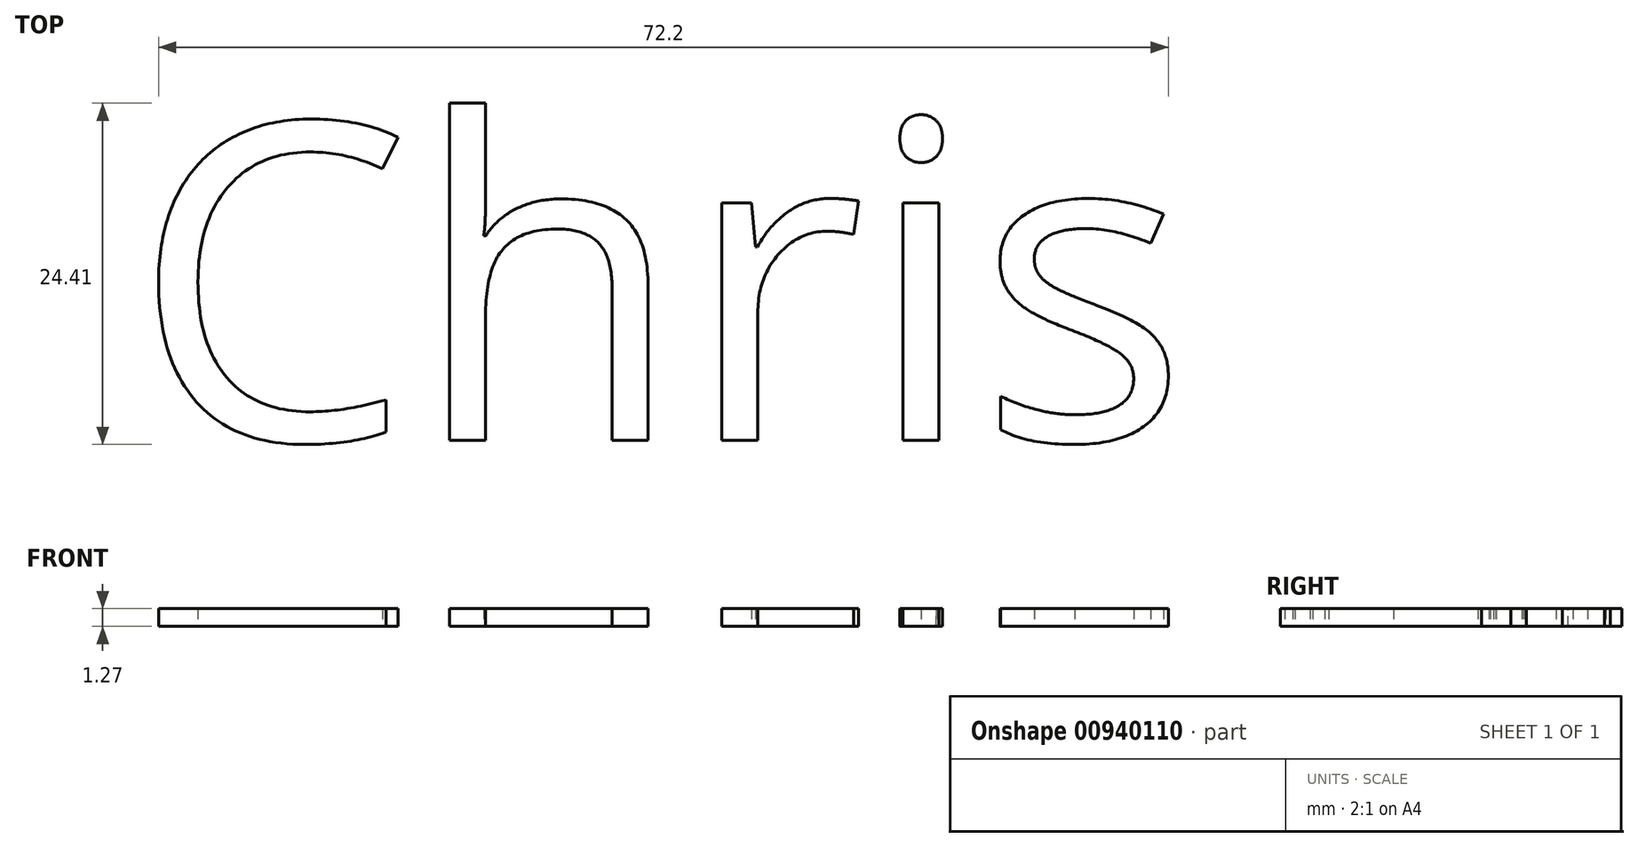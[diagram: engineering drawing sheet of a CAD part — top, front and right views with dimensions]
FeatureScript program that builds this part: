
annotation { "Feature Type Name" : "Feature", "Feature Type Description" : "" }
export const myFeature = defineFeature(function(context is Context, id is Id, definition is map)
    precondition{}
    {
        {
            var Q0;
            Q0=qCreatedBy(makeId("Top.planeOp"),FACE);
            var sketch = newSketch(context, id + "F0", { "sketchPlane" : qUnion([Q0])});
            skText(sketch, "E0", { "text": "Chris", "fontName": "OpenSans-Regular.ttf"});
            const initialGuessF0  = {"E0": [-0.02064, -0.01622, 1, 0, 0.02284]};
            skSetInitialGuess(sketch, initialGuessF0);
            skSolve(sketch);
        }
        {
            var Q0;
            Q0 = qSketchRegion(id + "F0", true);
            var Q1;
            Q1=makeQuery(id+"F0.imprint","IMPRINT",FACE,{"disambiguationData":[TD([[makeQuery(id+"F0.imprint","IMPRINT",EDGE,{"derivedFrom":sQuery(id+"F0.wireOp",EDGE,"E0.sketch_text.stroke-33")}),-1.0]])]});
            var Q2;
            Q2=makeQuery(id+"F0.imprint","IMPRINT",FACE,{"disambiguationData":[TD([[makeQuery(id+"F0.imprint","IMPRINT",EDGE,{"derivedFrom":sQuery(id+"F0.wireOp",EDGE,"E0.sketch_text.stroke-46")}),-1.0]])]});
            var Q3;
            Q3=makeQuery(id+"F0.imprint","IMPRINT",FACE,{"disambiguationData":[TD([[makeQuery(id+"F0.imprint","IMPRINT",EDGE,{"derivedFrom":sQuery(id+"F0.wireOp",EDGE,"E0.sketch_text.stroke-0")}),-1.0]])]});
            var Q4;
            Q4=makeQuery(id+"F0.imprint","IMPRINT",FACE,{"disambiguationData":[TD([[makeQuery(id+"F0.imprint","IMPRINT",EDGE,{"derivedFrom":sQuery(id+"F0.wireOp",EDGE,"E0.sketch_text.stroke-15")}),-1.0]])]});
            var Q5;
            Q5=makeQuery(id+"F0.imprint","IMPRINT",FACE,{"disambiguationData":[TD([[makeQuery(id+"F0.imprint","IMPRINT",EDGE,{"derivedFrom":sQuery(id+"F0.wireOp",EDGE,"E0.sketch_text.stroke-50")}),-1.0]])]});
            var Q6;
            Q6=makeQuery(id+"F0.imprint","IMPRINT",FACE,{"disambiguationData":[TD([[makeQuery(id+"F0.imprint","IMPRINT",EDGE,{"derivedFrom":sQuery(id+"F0.wireOp",EDGE,"E0.sketch_text.stroke-58")}),-1.0]])]});
            extrude(context, id + "F1", {"entities" : qUnion([Q0, Q1, Q2, Q3, Q4, Q5, Q6]), "depth" : 1.27 * mm, "offsetDistance" : 25.4 * mm});
        }
    });
